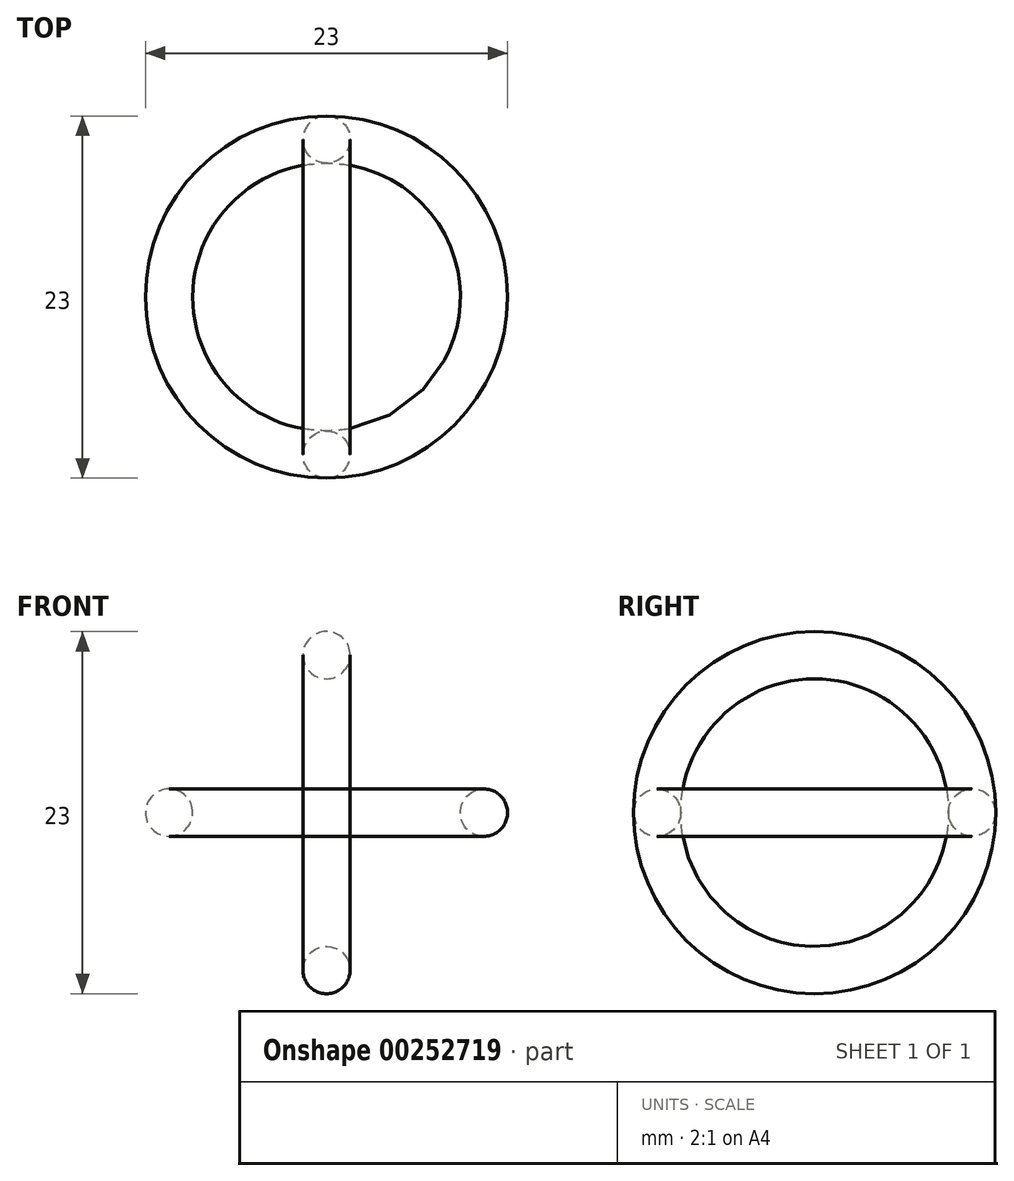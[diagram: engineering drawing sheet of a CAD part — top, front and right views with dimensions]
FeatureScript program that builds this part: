
annotation { "Feature Type Name" : "Feature", "Feature Type Description" : "" }
export const myFeature = defineFeature(function(context is Context, id is Id, definition is map)
    precondition{}
    {
        {
            var Q0;
            Q0=qCreatedBy(makeId("Top.planeOp"),FACE);
            var sketch = newSketch(context, id + "F0", { "sketchPlane" : qUnion([Q0])});
            skLineSegment(sketch, "E0.bottom", {"start": v(0, 0) * mm, "end": v(10, 0) * mm});
            skLineSegment(sketch, "E0.top", {"start": v(0, 10) * mm, "end": v(10, 10) * mm});
            skLineSegment(sketch, "E0.left", {"start": v(0, 0) * mm, "end": v(0, 10) * mm});
            skLineSegment(sketch, "E0.right", {"start": v(10, 0) * mm, "end": v(10, 10) * mm});
            skSolve(sketch);
        }
        {
            var Q0;
            Q0=qCreatedBy(makeId("Front.planeOp"),FACE);
            var sketch = newSketch(context, id + "F1", { "sketchPlane" : qUnion([Q0])});
            skLineSegment(sketch, "E1", {"start": v(0, 0) * mm, "end": v(10, 0) * mm, "construction": true});
            skLineSegment(sketch, "E2", {"start": v(0, 0) * mm, "end": v(0, 10) * mm, "construction": true});
            skCircle(sketch, "E3", {"center": v(0, 10) * mm, "radius": 1.5 * mm});
            skCircle(sketch, "E4", {"center": v(10, 0) * mm, "radius": 1.5 * mm});
            skSolve(sketch);
        }
        {
            var Q0;
            Q0=makeQuery(id+"F1.imprint","IMPRINT",FACE,{"disambiguationData":[TD([[makeQuery(id+"F1.imprint","IMPRINT",EDGE,{"derivedFrom":sQuery(id+"F1.wireOp",EDGE,"E3")}),1.0]])]});
            var Q1;
            Q1=sQuery(id+"F0.wireOp",EDGE,"E0.bottom");
            revolve(context, id + "F2", {"entities" : qUnion([Q0]), "axis" : qUnion([Q1]), "revolveType" : RevolveType.FULL});
        }
        {
            var Q0;
            Q0=makeQuery(id+"F1.imprint","IMPRINT",FACE,{"disambiguationData":[TD([[makeQuery(id+"F1.imprint","IMPRINT",EDGE,{"derivedFrom":sQuery(id+"F1.wireOp",EDGE,"E4")}),1.0]])]});
            var Q1;
            Q1=sQuery(id+"F1.wireOp",EDGE,"E2");
            revolve(context, id + "F3", {"entities" : qUnion([Q0]), "axis" : qUnion([Q1]), "revolveType" : RevolveType.FULL});
        }
    });
